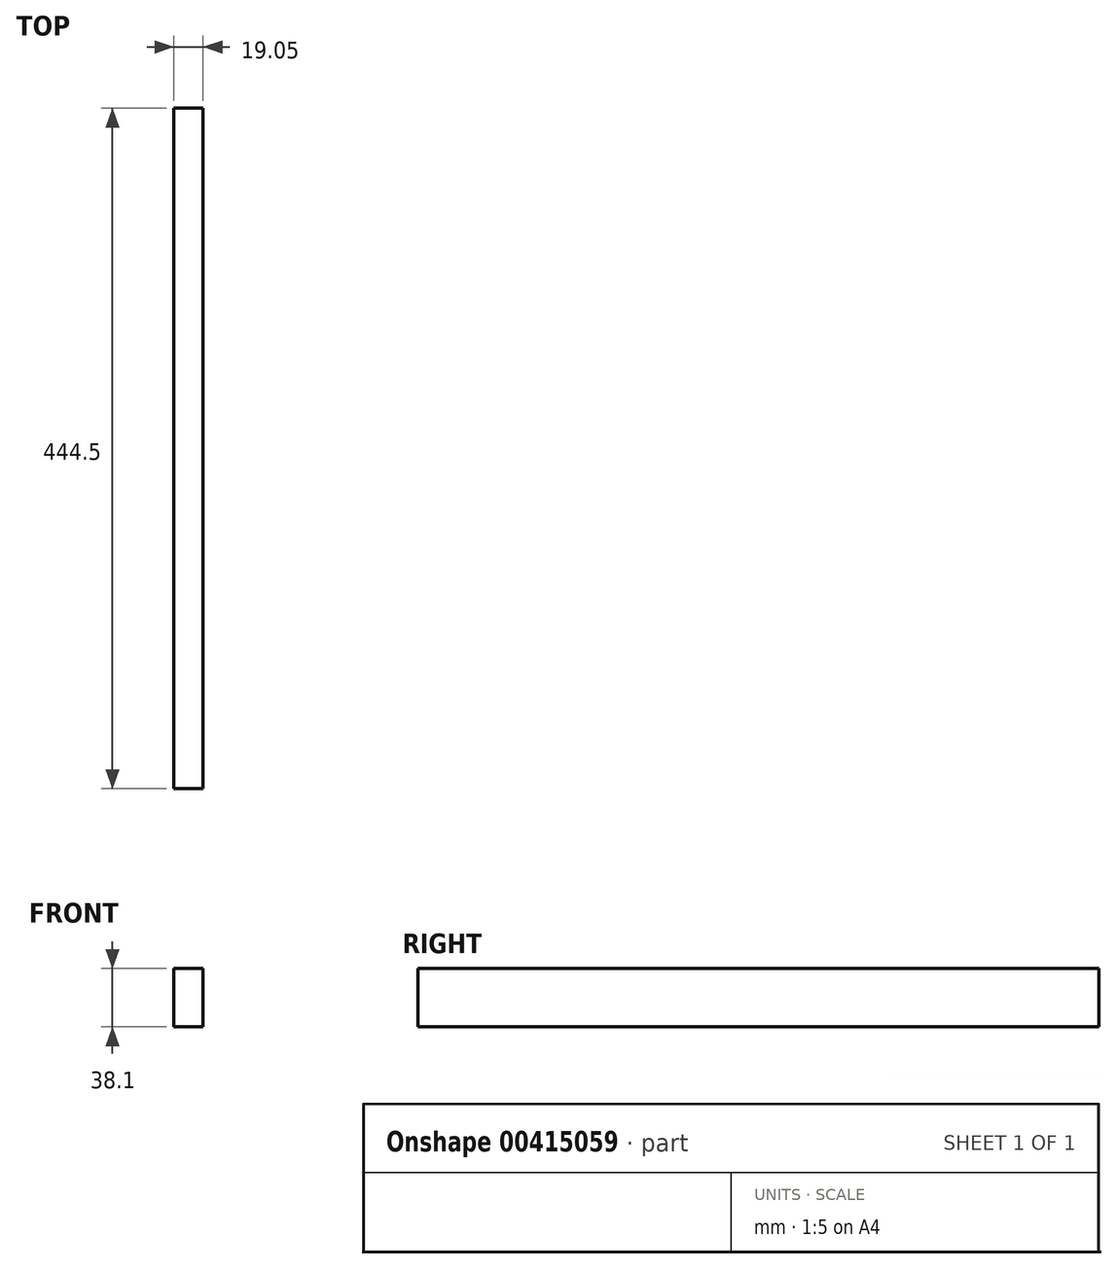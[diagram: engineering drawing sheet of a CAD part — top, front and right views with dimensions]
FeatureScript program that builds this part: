
annotation { "Feature Type Name" : "Feature", "Feature Type Description" : "" }
export const myFeature = defineFeature(function(context is Context, id is Id, definition is map)
    precondition{}
    {
        {
            var Q0;
            Q0=qCreatedBy(makeId("Front.planeOp"),FACE);
            var sketch = newSketch(context, id + "F0", { "sketchPlane" : qUnion([Q0])});
            skLineSegment(sketch, "E0.bottom", {"start": v(0, 0) * mm, "end": v(19.05, 0) * mm});
            skLineSegment(sketch, "E0.top", {"start": v(0, 38.1) * mm, "end": v(19.05, 38.1) * mm});
            skLineSegment(sketch, "E0.left", {"start": v(0, 0) * mm, "end": v(0, 38.1) * mm});
            skLineSegment(sketch, "E0.right", {"start": v(19.05, 0) * mm, "end": v(19.05, 38.1) * mm});
            skSolve(sketch);
        }
        {
            var Q0;
            Q0=makeQuery(id+"F0.imprint","IMPRINT",FACE,{"disambiguationData":[TD([[makeQuery(id+"F0.imprint","IMPRINT",EDGE,{"derivedFrom":sQuery(id+"F0.wireOp",EDGE,"E0.bottom")}),1.0]])]});
            extrude(context, id + "F1", {"entities" : qUnion([Q0]), "depth" : 444.5 * mm, "offsetDistance" : 25.4 * mm});
        }
    });
